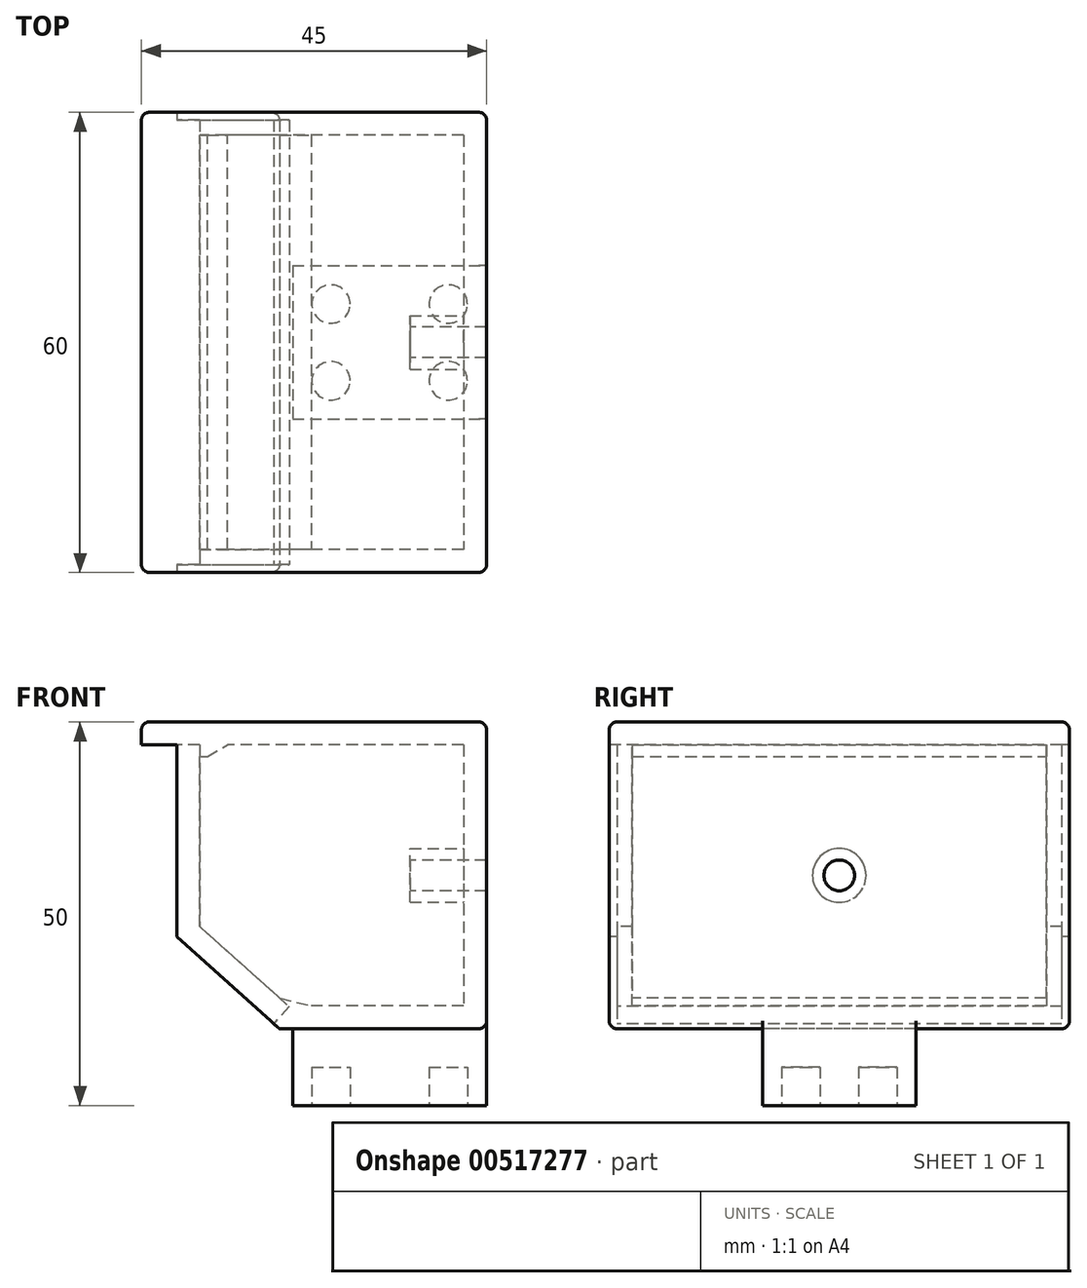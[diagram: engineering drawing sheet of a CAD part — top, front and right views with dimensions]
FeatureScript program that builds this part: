
annotation { "Feature Type Name" : "Feature", "Feature Type Description" : "" }
export const myFeature = defineFeature(function(context is Context, id is Id, definition is map)
    precondition{}
    {
        {
            var Q0;
            Q0=qCreatedBy(makeId("Top.planeOp"),FACE);
            var sketch = newSketch(context, id + "F0", { "sketchPlane" : qUnion([Q0])});
            skLineSegment(sketch, "E0.bottom", {"start": v(-12.65, 10) * mm, "end": v(12.65, 10) * mm});
            skLineSegment(sketch, "E0.top", {"start": v(-12.65, -10) * mm, "end": v(12.65, -10) * mm});
            skLineSegment(sketch, "E0.left", {"start": v(-12.65, 10) * mm, "end": v(-12.65, -10) * mm});
            skLineSegment(sketch, "E0.right", {"start": v(12.65, 10) * mm, "end": v(12.65, -10) * mm});
            skLineSegment(sketch, "E1", {"start": v(-12.65, 0) * mm, "end": v(12.65, 0) * mm, "construction": true});
            skLineSegment(sketch, "E2", {"start": v(0, 10) * mm, "end": v(0, -10) * mm, "construction": true});
            skSolve(sketch);
        }
        {
            var Q0;
            Q0 = qSketchRegion(id + "F0", true);
            extrude(context, id + "F1", {"entities" : qUnion([Q0]), "endBound" : BoundingType.SYMMETRIC, "depth" : 10 * mm, "offsetDistance" : 25 * mm});
        }
        {
            var Q0;
            Q0=makeQuery(id+"F1.opExtrude","CAP_FACE",FACE,{"disambiguationData":[OSD([sQuery(id+"F0.wireOp",EDGE,"E0.bottom"),sQuery(id+"F0.wireOp",EDGE,"E0.top"),sQuery(id+"F0.wireOp",EDGE,"E0.left"),sQuery(id+"F0.wireOp",EDGE,"E0.right")])],"isStart":true});
            var sketch = newSketch(context, id + "F2", { "sketchPlane" : qUnion([Q0])});
            skLineSegment(sketch, "E3.0", {"start": v(-7.65, 5) * mm, "end": v(-7.65, -5) * mm, "construction": true});
            skLineSegment(sketch, "E3.1", {"start": v(7.65, 5) * mm, "end": v(-7.65, 5) * mm, "construction": true});
            skLineSegment(sketch, "E3.2", {"start": v(7.65, -5) * mm, "end": v(7.65, 5) * mm, "construction": true});
            skLineSegment(sketch, "E3.3", {"start": v(-7.65, -5) * mm, "end": v(7.65, -5) * mm, "construction": true});
            skCircle(sketch, "E4", {"center": v(7.65, 5) * mm, "radius": 2.5 * mm});
            skCircle(sketch, "E5.MirrorC", {"center": v(7.65, -5) * mm, "radius": 2.5 * mm});
            skCircle(sketch, "E6.MirrorC", {"center": v(-7.65, -5) * mm, "radius": 2.5 * mm});
            skCircle(sketch, "E7.MirrorC", {"center": v(-7.65, 5) * mm, "radius": 2.5 * mm});
            skSolve(sketch);
        }
        {
            var Q0;
            Q0 = qSketchRegion(id + "F2", true);
            extrude(context, id + "F3", {"entities" : qUnion([Q0]), "operationType" : NewBodyOperationType.REMOVE, "oppositeDirection" : true, "depth" : 5 * mm, "offsetDistance" : 25 * mm});
        }
        {
            var Q0;
            Q0=makeQuery(id+"F1.opExtrude","CAP_FACE",FACE,{"disambiguationData":[OSD([sQuery(id+"F0.wireOp",EDGE,"E0.bottom"),sQuery(id+"F0.wireOp",EDGE,"E0.top"),sQuery(id+"F0.wireOp",EDGE,"E0.left"),sQuery(id+"F0.wireOp",EDGE,"E0.right")])],"isStart":false});
            var sketch = newSketch(context, id + "F4", { "sketchPlane" : qUnion([Q0])});
            skLineSegment(sketch, "E8.bottom", {"start": v(-32.35, 30) * mm, "end": v(12.65, 30) * mm});
            skLineSegment(sketch, "E8.top", {"start": v(-32.35, -30) * mm, "end": v(12.65, -30) * mm});
            skLineSegment(sketch, "E8.left", {"start": v(-32.35, 30) * mm, "end": v(-32.35, -30) * mm});
            skLineSegment(sketch, "E8.right", {"start": v(12.65, 30) * mm, "end": v(12.65, -30) * mm});
            skLineSegment(sketch, "E9", {"start": v(-32.35, 0) * mm, "end": v(12.65, 0) * mm, "construction": true});
            skSolve(sketch);
        }
        {
            var Q0;
            Q0 = qSketchRegion(id + "F4", true);
            extrude(context, id + "F5", {"entities" : qUnion([Q0]), "operationType" : NewBodyOperationType.ADD, "depth" : 40 * mm, "offsetDistance" : 25 * mm});
        }
        {
            var Q0;
            Q0=makeQuery(id+"F5.opExtrude","SWEPT_FACE",FACE,{"disambiguationData":[OSD([sQuery(id+"F4.wireOp",EDGE,"E8.left")])]});
            var sketch = newSketch(context, id + "F6", { "sketchPlane" : qUnion([Q0])});
            skLineSegment(sketch, "E10.0", {"start": v(-27, 8) * mm, "end": v(27, 8) * mm});
            skLineSegment(sketch, "E10.1", {"start": v(-27, 42) * mm, "end": v(-27, 8) * mm});
            skLineSegment(sketch, "E10.2", {"start": v(27, 42) * mm, "end": v(-27, 42) * mm});
            skLineSegment(sketch, "E10.3", {"start": v(27, 8) * mm, "end": v(27, 42) * mm});
            skSolve(sketch);
        }
        {
            var Q0;
            Q0=makeQuery(id+"F6.imprint","IMPRINT",FACE,{"disambiguationData":[TD([[makeQuery(id+"F6.imprint","IMPRINT",EDGE,{"derivedFrom":sQuery(id+"F6.wireOp",EDGE,"E10.0")}),1.0]])]});
            extrude(context, id + "F7", {"entities" : qUnion([Q0]), "operationType" : NewBodyOperationType.REMOVE, "oppositeDirection" : true, "depth" : 42 * mm, "offsetDistance" : 25 * mm});
        }
        {
            var Q0;
            Q0=makeQuery(id+"F5.opExtrude","SWEPT_FACE",FACE,{"disambiguationData":[OSD([sQuery(id+"F4.wireOp",EDGE,"E8.top")])]});
            var sketch = newSketch(context, id + "F8", { "sketchPlane" : qUnion([Q0])});
            skLineSegment(sketch, "E11", {"start": v(-32.35, 42) * mm, "end": v(-27.77, 42) * mm});
            skLineSegment(sketch, "E12", {"start": v(-27.77, 42) * mm, "end": v(-27.77, 17) * mm});
            skLineSegment(sketch, "E13", {"start": v(-27.77, 17) * mm, "end": v(-14.35, 5) * mm});
            skLineSegment(sketch, "E14", {"start": v(-14.35, 5) * mm, "end": v(-32.35, 5) * mm});
            skLineSegment(sketch, "E15", {"start": v(-32.35, 42) * mm, "end": v(-32.35, 5) * mm});
            skSolve(sketch);
        }
        {
            var Q0;
            Q0 = qSketchRegion(id + "F8", true);
            extrude(context, id + "F9", {"entities" : qUnion([Q0]), "operationType" : NewBodyOperationType.REMOVE, "oppositeDirection" : true, "depth" : 60 * mm, "offsetDistance" : 25 * mm});
        }
        {
            var Q0;
            Q0=makeQuery(id+"F9.boolean.opBoolean","COPY",FACE,{"disambiguationData":[TD([makeQuery(id+"F5.opExtrude","SWEPT_FACE",FACE,{"disambiguationData":[OSD([sQuery(id+"F4.wireOp",EDGE,"E8.bottom")])]})])],"derivedFrom":makeQuery(id+"F9.opExtrude","SWEPT_FACE",FACE,{"disambiguationData":[OSD([sQuery(id+"F8.wireOp",EDGE,"E12")])]})});
            var sketch = newSketch(context, id + "F10", { "sketchPlane" : qUnion([Q0])});
            skLineSegment(sketch, "E16.bottom", {"start": v(-29, 42) * mm, "end": v(29, 42) * mm});
            skLineSegment(sketch, "E16.top", {"start": v(-29, 17) * mm, "end": v(29, 17) * mm});
            skLineSegment(sketch, "E16.left", {"start": v(-29, 42) * mm, "end": v(-29, 17) * mm});
            skLineSegment(sketch, "E16.right", {"start": v(29, 42) * mm, "end": v(29, 17) * mm});
            skLineSegment(sketch, "E17.bottom", {"start": v(0, 42) * mm, "end": v(0, 42) * mm});
            skLineSegment(sketch, "E17.top", {"start": v(0, 17) * mm, "end": v(0, 17) * mm});
            skLineSegment(sketch, "E17.left", {"start": v(0, 42) * mm, "end": v(0, 17) * mm, "construction": true});
            skLineSegment(sketch, "E17.right", {"start": v(0, 42) * mm, "end": v(0, 17) * mm, "construction": true});
            skSolve(sketch);
        }
        {
            var Q0;
            Q0 = qSketchRegion(id + "F10", true);
            extrude(context, id + "F11", {"entities" : qUnion([Q0]), "operationType" : NewBodyOperationType.REMOVE, "oppositeDirection" : true, "depth" : 3 * mm, "offsetDistance" : 25 * mm});
        }
        {
            var Q0;
            Q0=makeQuery(id+"F9.boolean.opBoolean","COPY",FACE,{"derivedFrom":makeQuery(id+"F9.opExtrude","SWEPT_FACE",FACE,{"disambiguationData":[OSD([sQuery(id+"F8.wireOp",EDGE,"E13")])]})});
            var sketch = newSketch(context, id + "F12", { "sketchPlane" : qUnion([Q0])});
            skLineSegment(sketch, "E18.bottom", {"start": v(-32.03, -29) * mm, "end": v(-15.03, -29) * mm});
            skLineSegment(sketch, "E18.top", {"start": v(-32.03, 29) * mm, "end": v(-15.03, 29) * mm});
            skLineSegment(sketch, "E18.right", {"start": v(-15.03, -29) * mm, "end": v(-15.03, 29) * mm});
            skLineSegment(sketch, "E19", {"start": v(-35.76, 0) * mm, "end": v(-15.03, 0) * mm, "construction": true});
            skLineSegment(sketch, "E20", {"start": v(-32.03, -29) * mm, "end": v(-32.03, 29) * mm});
            skSolve(sketch);
        }
        {
            var Q0;
            Q0 = qSketchRegion(id + "F12", true);
            extrude(context, id + "F13", {"entities" : qUnion([Q0]), "operationType" : NewBodyOperationType.REMOVE, "oppositeDirection" : true, "depth" : 3 * mm, "offsetDistance" : 25 * mm});
        }
        {
            var Q0;
            Q0=makeQuery(id+"F5.opExtrude","SWEPT_EDGE",EDGE,{"disambiguationData":[OSD([sQuery(id+"F4.wireOp",EDGE,"E8.top"),sQuery(id+"F4.wireOp",EDGE,"E8.right")])]});
            var Q1;
            Q1=makeQuery(id+"F5.opExtrude","CAP_EDGE",EDGE,{"disambiguationData":[OSD([sQuery(id+"F4.wireOp",EDGE,"E8.top")])],"isStart":false});
            var Q2;
            Q2=makeQuery(id+"F5.opExtrude","CAP_EDGE",EDGE,{"disambiguationData":[OSD([sQuery(id+"F4.wireOp",EDGE,"E8.right")])],"isStart":false});
            var Q3;
            Q3=makeQuery(id+"F5.opExtrude","SWEPT_EDGE",EDGE,{"disambiguationData":[OSD([sQuery(id+"F4.wireOp",EDGE,"E8.bottom"),sQuery(id+"F4.wireOp",EDGE,"E8.right")])]});
            var Q4;
            Q4=makeQuery(id+"F5.opExtrude","CAP_EDGE",EDGE,{"disambiguationData":[OSD([sQuery(id+"F4.wireOp",EDGE,"E8.bottom")])],"isStart":false});
            fillet(context, id + "F14", {"entities" : qUnion([Q0, Q1, Q2, Q3, Q4]), "radius" : 1 * mm, "tangentPropagation" : true, "allowEdgeOverflow" : false});
        }
        {
            var Q0;
            Q0=makeQuery(id+"F9.boolean.opBoolean","MERGE",EDGE,{"derivedFrom":[makeQuery(id+"F7.boolean.opBoolean","COPY",EDGE,{"derivedFrom":makeQuery(id+"F7.opExtrude","CAP_EDGE",EDGE,{"disambiguationData":[OSD([sQuery(id+"F6.wireOp",EDGE,"E10.2")])],"isStart":true})}),makeQuery(id+"F9.opExtrude","SWEPT_EDGE",EDGE,{"disambiguationData":[OSD([sQuery(id+"F4.wireOp",EDGE,"E8.top"),sQuery(id+"F4.wireOp",EDGE,"E8.left"),sQuery(id+"F8.wireOp",EDGE,"E11"),sQuery(id+"F8.wireOp",EDGE,"E15")])]})]});
            var Q1;
            Q1=makeQuery(id+"F5.opExtrude","CAP_EDGE",EDGE,{"disambiguationData":[OSD([sQuery(id+"F4.wireOp",EDGE,"E8.left")])],"isStart":false});
            var Q2;
            Q2=makeQuery(id+"F5.opExtrude","CAP_EDGE",EDGE,{"disambiguationData":[OSD([sQuery(id+"F4.wireOp",EDGE,"E8.top")])],"isStart":true});
            var Q3;
            Q3=makeQuery(id+"F5.opExtrude","CAP_EDGE",EDGE,{"disambiguationData":[OSD([sQuery(id+"F4.wireOp",EDGE,"E8.bottom")])],"isStart":true});
            fillet(context, id + "F15", {"entities" : qUnion([Q0, Q1, Q2, Q3]), "radius" : 1 * mm, "tangentPropagation" : true, "allowEdgeOverflow" : false});
        }
        {
            var Q0;
            Q0=makeQuery(id+"F7.boolean.opBoolean","COPY",FACE,{"derivedFrom":makeQuery(id+"F7.opExtrude","SWEPT_FACE",FACE,{"disambiguationData":[OSD([sQuery(id+"F6.wireOp",EDGE,"E10.1")])]})});
            var sketch = newSketch(context, id + "F16", { "sketchPlane" : qUnion([Q0])});
            skLineSegment(sketch, "E21", {"start": v(-24.77, 42) * mm, "end": v(-24.77, 40.5) * mm});
            skLineSegment(sketch, "E22", {"start": v(-24.77, 40.5) * mm, "end": v(-23.77, 40.5) * mm});
            skLineSegment(sketch, "E23", {"start": v(-23.77, 40.5) * mm, "end": v(-21.17, 42) * mm});
            skLineSegment(sketch, "E24", {"start": v(-21.17, 42) * mm, "end": v(-24.77, 42) * mm});
            skSolve(sketch);
        }
        {
            var Q0;
            Q0 = qSketchRegion(id + "F16", true);
            extrude(context, id + "F17", {"entities" : qUnion([Q0]), "operationType" : NewBodyOperationType.ADD, "depth" : 55 * mm, "offsetDistance" : 25 * mm});
        }
        {
            var Q0;
            Q0=makeQuery(id+"F5.boolean.opBoolean","MERGE",FACE,{"derivedFrom":[makeQuery(id+"F1.opExtrude","SWEPT_FACE",FACE,{"disambiguationData":[OSD([sQuery(id+"F0.wireOp",EDGE,"E0.right")])]}),makeQuery(id+"F5.opExtrude","SWEPT_FACE",FACE,{"disambiguationData":[OSD([sQuery(id+"F4.wireOp",EDGE,"E8.right")])]})]});
            var sketch = newSketch(context, id + "F18", { "sketchPlane" : qUnion([Q0])});
            skLineSegment(sketch, "E25", {"start": v(0, 44) * mm, "end": v(0, -5) * mm, "construction": true});
            skLineSegment(sketch, "E26", {"start": v(-29, 25) * mm, "end": v(29, 25) * mm, "construction": true});
            skCircle(sketch, "E27", {"center": v(0, 25) * mm, "radius": 3.5 * mm});
            skSolve(sketch);
        }
        {
            var Q0;
            Q0 = qSketchRegion(id + "F18", true);
            extrude(context, id + "F19", {"entities" : qUnion([Q0]), "operationType" : NewBodyOperationType.ADD, "oppositeDirection" : true, "depth" : 10 * mm, "offsetDistance" : 25 * mm});
        }
        {
            var Q0;
            Q0=makeQuery(id+"F19.opExtrude","CAP_FACE",FACE,{"disambiguationData":[OSD([sQuery(id+"F18.wireOp",EDGE,"E27")])],"isStart":false});
            var sketch = newSketch(context, id + "F20", { "sketchPlane" : qUnion([Q0])});
            skCircle(sketch, "E28", {"center": v(0, 25) * mm, "radius": 2 * mm});
            skSolve(sketch);
        }
        {
            var Q0;
            Q0 = qSketchRegion(id + "F20", true);
            extrude(context, id + "F21", {"entities" : qUnion([Q0]), "operationType" : NewBodyOperationType.REMOVE, "oppositeDirection" : true, "depth" : 25 * mm, "offsetDistance" : 25 * mm});
        }
        {
            var Q0;
            Q0=makeQuery(id+"F7.boolean.opBoolean","COPY",FACE,{"derivedFrom":makeQuery(id+"F7.opExtrude","SWEPT_FACE",FACE,{"disambiguationData":[OSD([sQuery(id+"F6.wireOp",EDGE,"E10.3")])]})});
            var sketch = newSketch(context, id + "F22", { "sketchPlane" : qUnion([Q0])});
            skLineSegment(sketch, "E29", {"start": v(14.32, 9) * mm, "end": v(13.2, 8) * mm});
            skLineSegment(sketch, "E30", {"start": v(13.2, 8) * mm, "end": v(10.2, 8) * mm});
            skLineSegment(sketch, "E31", {"start": v(10.2, 8) * mm, "end": v(14.32, 9) * mm});
            skSolve(sketch);
        }
        {
            var Q0;
            Q0 = qSketchRegion(id + "F22", true);
            extrude(context, id + "F23", {"entities" : qUnion([Q0]), "operationType" : NewBodyOperationType.ADD, "depth" : 55 * mm, "offsetDistance" : 25 * mm});
        }
    });
